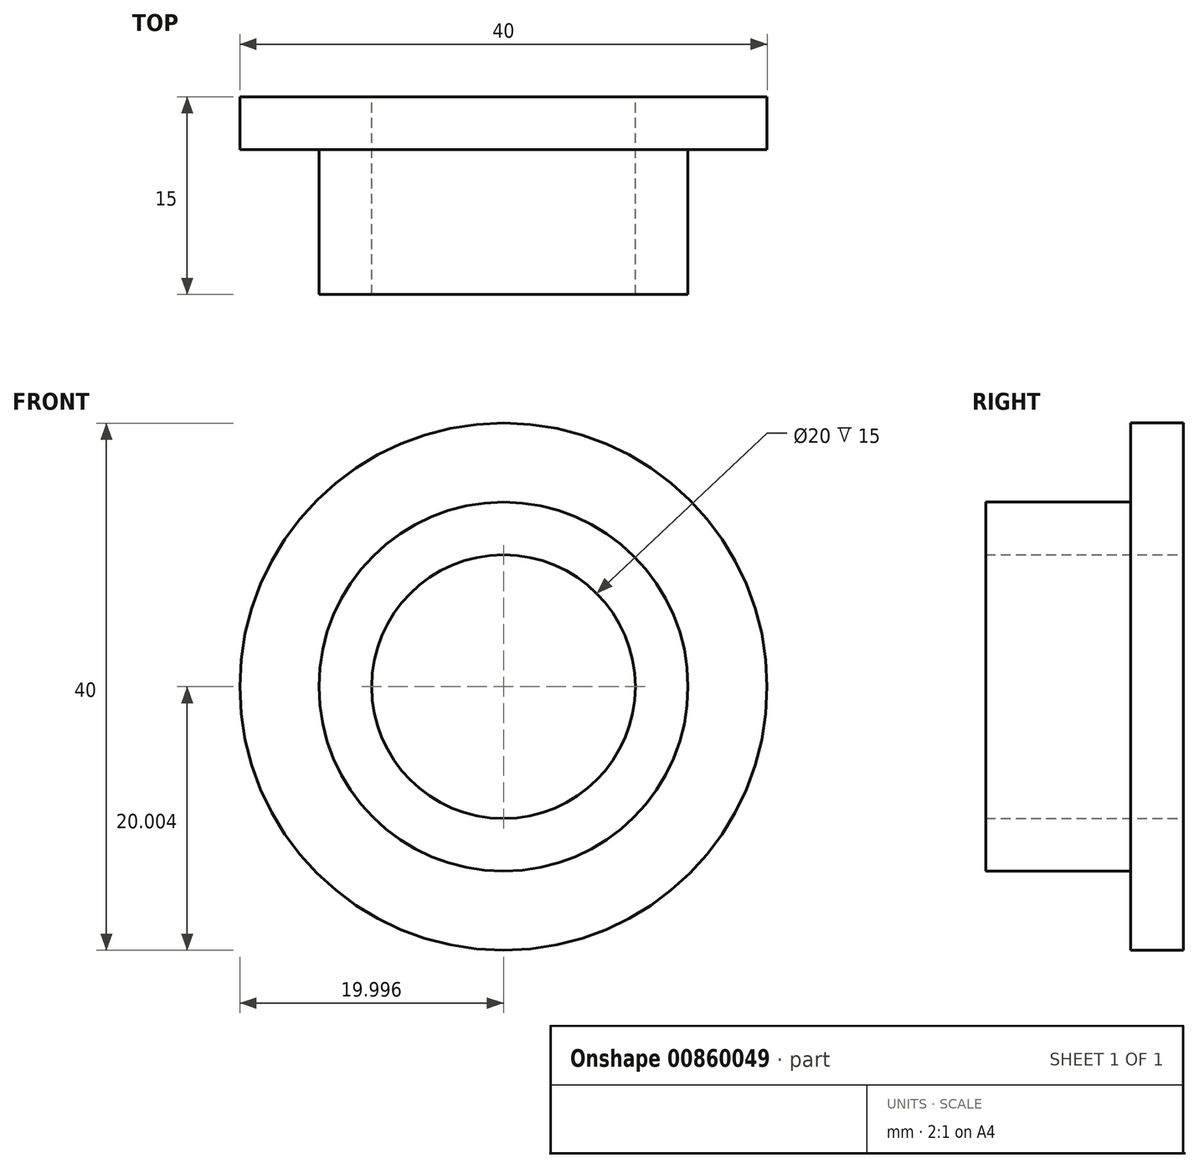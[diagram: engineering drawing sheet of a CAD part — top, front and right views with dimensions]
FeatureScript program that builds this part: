
annotation { "Feature Type Name" : "Feature", "Feature Type Description" : "" }
export const myFeature = defineFeature(function(context is Context, id is Id, definition is map)
    precondition{}
    {
        {
            var Q0;
            Q0=qCreatedBy(makeId("Front.planeOp"),FACE);
            var sketch = newSketch(context, id + "F0", { "sketchPlane" : qUnion([Q0])});
            skCircle(sketch, "E0", {"center": v(14.24, 16.9) * mm, "radius": 14 * mm});
            skLineSegment(sketch, "E1", {"start": v(25.66, 3.64) * mm, "end": v(25.66, 3.64) * mm});
            skCircle(sketch, "E2", {"center": v(14.24, 16.9) * mm, "radius": 10 * mm});
            skCircle(sketch, "E3", {"center": v(14.24, 16.9) * mm, "radius": 20 * mm});
            skSolve(sketch);
        }
        {
            var Q0;
            Q0=makeQuery(id+"F0.imprint","IMPRINT",FACE,{"disambiguationData":[TD([[makeQuery(id+"F0.imprint","IMPRINT",EDGE,{"derivedFrom":sQuery(id+"F0.wireOp",EDGE,"E0")}),-1.0]])]});
            extrude(context, id + "F1", {"entities" : qUnion([Q0]), "depth" : 4 * mm, "offsetDistance" : 25 * mm});
        }
        {
            var Q0;
            Q0=makeQuery(id+"F0.imprint","IMPRINT",FACE,{"disambiguationData":[TD([[makeQuery(id+"F0.imprint","IMPRINT",EDGE,{"derivedFrom":sQuery(id+"F0.wireOp",EDGE,"E0")}),1.0]])]});
            extrude(context, id + "F2", {"entities" : qUnion([Q0]), "operationType" : NewBodyOperationType.ADD, "depth" : 15 * mm, "offsetDistance" : 25 * mm});
        }
    });
